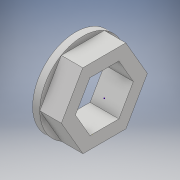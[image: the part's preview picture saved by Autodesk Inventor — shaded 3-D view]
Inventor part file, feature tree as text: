
AUTODESK INVENTOR PART (.ipt)
format: ipt  version: 2018 (Build 220112000, 112)  size: 129,024 bytes
history: native  units: mm
features: sketch x5, extrude x3
ambient origin geometry x8: Origin, YZ Plane, XZ Plane, XY Plane, X Axis, Y Axis, Z Axis, Center Point
bodies: Solid1 (feature_tree)
feature tree (8):
  extrude  "Extrusion1"  Depth=3.0mm
  sketch  "Sketch2"  dims[d2=3.0mm d3=0.0mm d4=1.0mm d5=0.0mm]
  extrude  "Extrusion2"  Depth=1.0mm TaperAngle=0.0deg
  sketch  "Sketch4"
  extrude  "Extrusion3"  [1 undecoded]
  sketch  "Sketch1"  dims[d0=3.0mm d1=3.0mm]
  sketch  "Sketch3"  dims[d6=10.0mm d7=0.0mm]
  sketch  "Sketch5"
note: 1 required parameter value undecoded (feature->parameter linkage not recoverable at this tier; creation-order binding heuristic only, values carry confidence <= 0.55)
